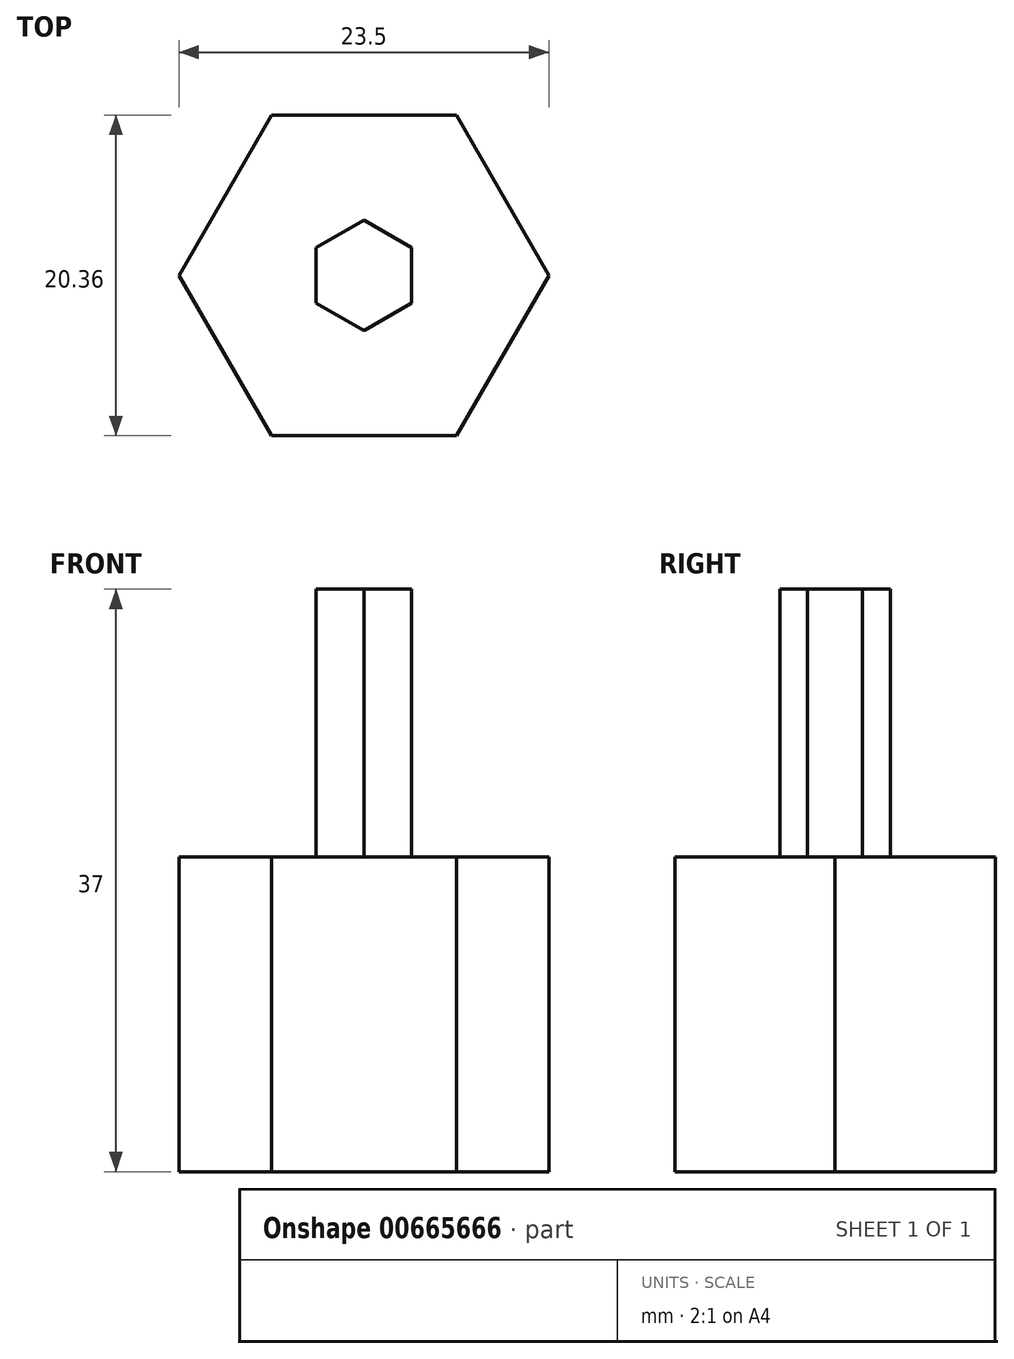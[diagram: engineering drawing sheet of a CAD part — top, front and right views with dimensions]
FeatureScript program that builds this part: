
annotation { "Feature Type Name" : "Feature", "Feature Type Description" : "" }
export const myFeature = defineFeature(function(context is Context, id is Id, definition is map)
    precondition{}
    {
        {
            var Q0;
            Q0=qCreatedBy(makeId("Top.planeOp"),FACE);
            var sketch = newSketch(context, id + "F0", { "sketchPlane" : qUnion([Q0])});
            skCircle(sketch, "E0.cCircle", {"center": v(0, 0) * mm, "radius": 11.75 * mm, "construction": true});
            skLineSegment(sketch, "E0.0", {"start": v(5.87, -10.18) * mm, "end": v(-5.87, -10.18) * mm});
            skLineSegment(sketch, "E0.1", {"start": v(-5.87, -10.18) * mm, "end": v(-11.75, 0) * mm});
            skLineSegment(sketch, "E0.2", {"start": v(-11.75, 0) * mm, "end": v(-5.87, 10.18) * mm});
            skLineSegment(sketch, "E0.3", {"start": v(-5.87, 10.18) * mm, "end": v(5.88, 10.18) * mm});
            skLineSegment(sketch, "E0.4", {"start": v(5.88, 10.18) * mm, "end": v(11.75, 0) * mm});
            skLineSegment(sketch, "E0.5", {"start": v(11.75, 0) * mm, "end": v(5.87, -10.18) * mm});
            skSolve(sketch);
        }
        {
            var Q0;
            Q0=makeQuery(id+"F0.imprint","IMPRINT",FACE,{"disambiguationData":[TD([[makeQuery(id+"F0.imprint","IMPRINT",EDGE,{"derivedFrom":sQuery(id+"F0.wireOp",EDGE,"E0.0")}),-1.0]])]});
            extrude(context, id + "F1", {"entities" : qUnion([Q0]), "depth" : 20 * mm, "offsetDistance" : 25 * mm});
        }
        {
            var Q0;
            Q0=makeQuery(id+"F1.opExtrude","CAP_FACE",FACE,{"disambiguationData":[OSD([sQuery(id+"F0.wireOp",EDGE,"E0.0"),sQuery(id+"F0.wireOp",EDGE,"E0.1"),sQuery(id+"F0.wireOp",EDGE,"E0.2"),sQuery(id+"F0.wireOp",EDGE,"E0.3"),sQuery(id+"F0.wireOp",EDGE,"E0.4"),sQuery(id+"F0.wireOp",EDGE,"E0.5")])],"isStart":false});
            var sketch = newSketch(context, id + "F2", { "sketchPlane" : qUnion([Q0])});
            skCircle(sketch, "E1.cCircle", {"center": v(0, 0) * mm, "radius": 3.5 * mm, "construction": true});
            skLineSegment(sketch, "E1.0", {"start": v(3.03, 1.75) * mm, "end": v(3.03, -1.75) * mm});
            skLineSegment(sketch, "E1.1", {"start": v(3.03, -1.75) * mm, "end": v(0, -3.5) * mm});
            skLineSegment(sketch, "E1.2", {"start": v(0, -3.5) * mm, "end": v(-3.03, -1.75) * mm});
            skLineSegment(sketch, "E1.3", {"start": v(-3.03, -1.75) * mm, "end": v(-3.03, 1.75) * mm});
            skLineSegment(sketch, "E1.4", {"start": v(-3.03, 1.75) * mm, "end": v(0, 3.5) * mm});
            skLineSegment(sketch, "E1.5", {"start": v(0, 3.5) * mm, "end": v(3.03, 1.75) * mm});
            skSolve(sketch);
        }
        {
            var Q0;
            Q0=makeQuery(id+"F2.imprint","IMPRINT",FACE,{"disambiguationData":[TD([[makeQuery(id+"F2.imprint","IMPRINT",EDGE,{"derivedFrom":sQuery(id+"F2.wireOp",EDGE,"E1.0")}),-1.0]])]});
            extrude(context, id + "F3", {"entities" : qUnion([Q0]), "operationType" : NewBodyOperationType.ADD, "depth" : 17 * mm, "offsetDistance" : 25 * mm});
        }
    });
